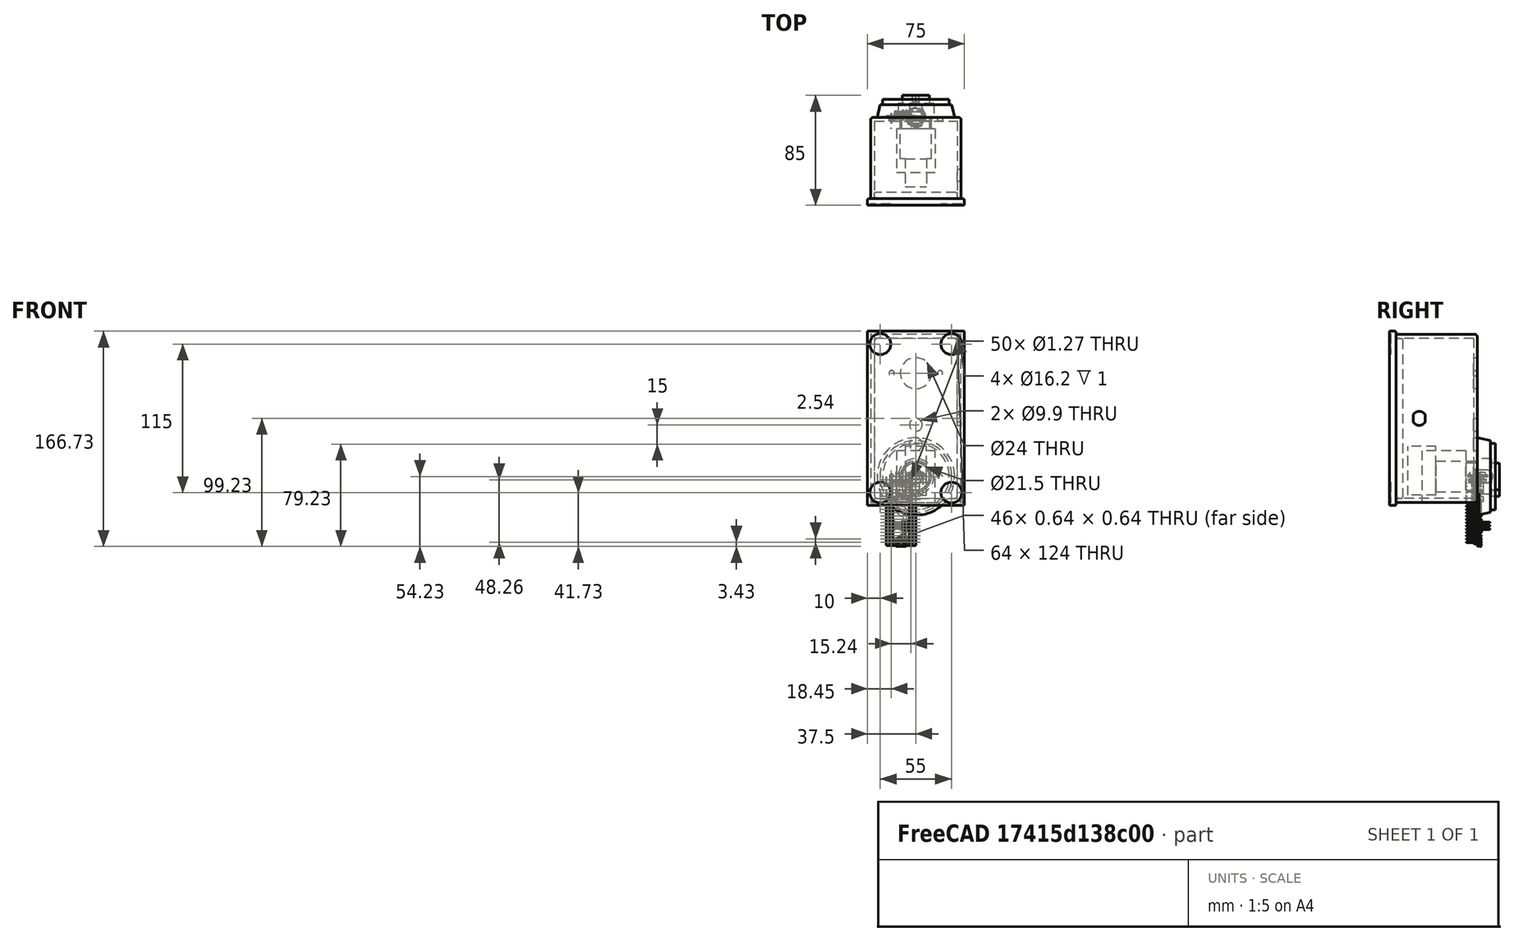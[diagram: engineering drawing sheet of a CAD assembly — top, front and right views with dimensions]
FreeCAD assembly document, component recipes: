
FREECAD ASSEMBLY — COMPONENT RECIPES ("PDU")

This assembly document has 3 components, labeled P0..P2 below (a component is one placed body or linked part). 3 of them carry a construction recipe — the FreeCAD feature program that regenerates the part from scratch, quoted from this document or its linked companion documents; the rest are supplied as boundary geometry only. No exploded tour is included for this assembly.
COMPONENT P0 — recipe-attached ("Rubber", modeled in this document).
Construction recipe (the document's own serialized feature program — sketch geometry with constraints, then the solid features built on it; lengths are millimeters unless a unit is written):

FEATURE [Sketcher::SketchObject] Sketch011
  ArcFitTolerance = 1e-06
  AttachmentSupport = -> [XY_Plane010]
  FullyConstrained = true
  MakeInternals = false
  MapMode = 5
  sketch-geometry (2):
    g0: Circle CenterX=0 CenterY=0 CenterZ=0 NormalX=0 NormalY=0 NormalZ=1 AngleXU=0 Radius=7.75
    g1: Circle CenterX=0 CenterY=0 CenterZ=0 NormalX=0 NormalY=0 NormalZ=1 AngleXU=0 Radius=5.4
  constraints (4):
    c: Diameter(g0) = 15.5
    c: Coincident(g0,g-1)
    c: Diameter(g1) = 10.8
    c: Coincident(g1,g0)
FEATURE [PartDesign::Pad] Pad007
  Direction = (0,0,1)
  Length = 1
  Length2 = 10
  Profile = -> Sketch011
  ReferenceAxis = -> Sketch011 [N_Axis]
  Refine = true
  Suppressed = false
  Type = 0
FEATURE [PartDesign::Body] Body004  label="Rubber"
  AllowCompound = false
  Group = -> [Sketch011,Pad007]
  Origin = -> Origin010
  Tip = -> Pad007
COMPONENT P1 — recipe-attached ("House", modeled in this document).
Construction recipe (the document's own serialized feature program — sketch geometry with constraints, then the solid features built on it; lengths are millimeters unless a unit is written):

FEATURE [Sketcher::SketchObject] Sketch012
  ArcFitTolerance = 1e-06
  FullyConstrained = false
  MakeInternals = false
  sketch-geometry (8):
    g0: ArcOfCircle CenterX=0 CenterY=0 CenterZ=0 NormalX=0 NormalY=0 NormalZ=1 AngleXU=0 Radius=5.4 StartAngle=2.12208 EndAngle=3.14159
    g1: LineSegment StartX=0 StartY=4.6 StartZ=0 EndX=2.82843 EndY=4.6 EndZ=0
    g2: LineSegment StartX=0 StartY=4.6 StartZ=0 EndX=-2.82843 EndY=4.6 EndZ=0
    g3: ArcOfCircle CenterX=0 CenterY=0 CenterZ=0 NormalX=0 NormalY=0 NormalZ=1 AngleXU=0 Radius=5.4 StartAngle=-9e-16 EndAngle=1.01951
    g4: ArcOfCircle CenterX=0 CenterY=0 CenterZ=0 NormalX=0 NormalY=0 NormalZ=1 AngleXU=0 Radius=5.4 StartAngle=3.14159 EndAngle=4.1611
    g5: LineSegment StartX=0 StartY=-4.6 StartZ=0 EndX=-2.82843 EndY=-4.6 EndZ=0
    g6: LineSegment StartX=0 StartY=-4.6 StartZ=0 EndX=2.82843 EndY=-4.6 EndZ=0
    g7: ArcOfCircle CenterX=0 CenterY=0 CenterZ=0 NormalX=0 NormalY=0 NormalZ=1 AngleXU=0 Radius=5.4 StartAngle=5.26367 EndAngle=6.28319
  constraints (14):
    c: Diameter(g0) = 10.8
    c: Coincident(g0,g-1)
    c: PointOnObject(g1,g-2)
    c: Horizontal(g1)
    c: Coincident(g1,g3)
    c: Coincident(g2,g0)
    c: Equal(g0,g3)
    c: Coincident(g0,g3)
    c: Diameter(g4) = 10.8
    c: Horizontal(g6)
    c: Coincident(g6,g7)
    c: Coincident(g5,g4)
    c: Equal(g4,g7)
    c: Coincident(g4,g7)
FEATURE [PartDesign::Pad] Pad008
  Direction = (0,0,1)
  Length = 1
  Length2 = 10
  Profile = -> Sketch012
  ReferenceAxis = -> Sketch012 [N_Axis]
  Refine = true
  Suppressed = false
  Type = 0
FEATURE [Sketcher::SketchObject] Sketch013
  ArcFitTolerance = 1e-06
  FullyConstrained = false
  MakeInternals = false
  sketch-geometry (8):
    g0: ArcOfCircle CenterX=0 CenterY=0 CenterZ=0 NormalX=0 NormalY=0 NormalZ=1 AngleXU=0 Radius=5.4 StartAngle=2.12208 EndAngle=3.14159
    g1: LineSegment StartX=0 StartY=4.6 StartZ=0 EndX=2.82843 EndY=4.6 EndZ=0
    g2: LineSegment StartX=0 StartY=4.6 StartZ=0 EndX=-2.82843 EndY=4.6 EndZ=0
    g3: ArcOfCircle CenterX=0 CenterY=0 CenterZ=0 NormalX=0 NormalY=0 NormalZ=1 AngleXU=0 Radius=5.4 StartAngle=-9e-16 EndAngle=1.01951
    g4: ArcOfCircle CenterX=0 CenterY=0 CenterZ=0 NormalX=0 NormalY=0 NormalZ=1 AngleXU=0 Radius=5.4 StartAngle=3.14159 EndAngle=4.1611
    g5: LineSegment StartX=0 StartY=-4.6 StartZ=0 EndX=-2.82843 EndY=-4.6 EndZ=0
    g6: LineSegment StartX=0 StartY=-4.6 StartZ=0 EndX=2.82843 EndY=-4.6 EndZ=0
    g7: ArcOfCircle CenterX=0 CenterY=0 CenterZ=0 NormalX=0 NormalY=0 NormalZ=1 AngleXU=0 Radius=5.4 StartAngle=5.26367 EndAngle=6.28319
  constraints (14):
    c: Diameter(g0) = 10.8
    c: Coincident(g0,g-1)
    c: PointOnObject(g1,g-2)
    c: Horizontal(g1)
    c: Coincident(g1,g3)
    c: Coincident(g2,g0)
    c: Equal(g0,g3)
    c: Coincident(g0,g3)
    c: Diameter(g4) = 10.8
    c: Horizontal(g6)
    c: Coincident(g6,g7)
    c: Coincident(g5,g4)
    c: Equal(g4,g7)
    c: Coincident(g4,g7)
FEATURE [PartDesign::Pad] Pad009
  BaseFeature = -> Pad008
  Direction = (0,0,1)
  Length = 13.1
  Length2 = 10
  Profile = -> Sketch013
  ReferenceAxis = -> Sketch013 [N_Axis]
  Refine = true
  Reversed = true
  Suppressed = false
  Type = 0
FEATURE [Sketcher::SketchObject] Sketch014
  ArcFitTolerance = 1e-06
  AttachmentSupport = -> [YZ_Plane012]
  FullyConstrained = true
  MakeInternals = false
  MapMode = 5
  Placement = pos=(0,0,0) rot=(0.57735,0.57735,0.57735;2.0944rad)
  sketch-geometry (5):
    g0: LineSegment [constr] StartX=0 StartY=0 StartZ=0 EndX=0 EndY=1 EndZ=0
    g1: LineSegment StartX=0 StartY=1 StartZ=0 EndX=0 EndY=3 EndZ=0
    g2: LineSegment StartX=0 StartY=3 StartZ=0 EndX=5.9 EndY=3 EndZ=0
    g3: LineSegment StartX=0 StartY=1 StartZ=0 EndX=6.9 EndY=1 EndZ=0
    g4: LineSegment StartX=6.9 StartY=1 StartZ=0 EndX=5.9 EndY=3 EndZ=0
  constraints (14):
    c: Distance(g0) = 1
    c: Coincident(g0,g-1)
    c: PointOnObject(g0,g-2)
    c: Distance(g1) = 2
    c: Coincident(g1,g0)
    c: PointOnObject(g1,g-2)
    c: Distance(g2) = 5.9
    c: Coincident(g2,g1)
    c: Horizontal(g2)
    c: Distance(g3) = 6.9
    c: Coincident(g3,g0)
    c: Horizontal(g3)
    c: Coincident(g4,g3)
    c: Coincident(g4,g2)
FEATURE [PartDesign::Revolution] Revolution002
  Angle = 360
  Angle2 = 60
  Axis = (0,0,1)
  Base = (0,0,0)
  BaseFeature = -> Pad009
  Profile = -> Sketch014
  ReferenceAxis = -> Sketch014 [V_Axis]
  Refine = true
  Reversed = true
  Suppressed = false
  Type = 0
FEATURE [Sketcher::SketchObject] Sketch015
  ArcFitTolerance = 1e-06
  AttachmentSupport = -> [Revolution002]
  FullyConstrained = false
  MakeInternals = false
  MapMode = 5
  Placement = pos=(0,0,3) rot=(0,0,1;0rad)
  sketch-geometry (4):
    g0: ArcOfCircle CenterX=-3.315 CenterY=-8.55e-14 CenterZ=0 NormalX=0 NormalY=0 NormalZ=1 AngleXU=0 Radius=1.28 StartAngle=1.5708 EndAngle=4.71239
    g1: ArcOfCircle CenterX=3.315 CenterY=-8.55e-14 CenterZ=0 NormalX=0 NormalY=0 NormalZ=1 AngleXU=0 Radius=1.28 StartAngle=4.71239 EndAngle=7.85398
    g2: LineSegment StartX=-3.315 StartY=1.28 StartZ=0 EndX=3.315 EndY=1.28 EndZ=0
    g3: LineSegment StartX=-3.315 StartY=-1.28 StartZ=0 EndX=3.315 EndY=-1.28 EndZ=0
  constraints (9):
    c: PointOnObject(g0,g-1)
    c: Tangent(g0,g2) = 1.5708
    c: Tangent(g0,g3) = -1.5708
    c: Tangent(g1,g2) = 1.5708
    c: Tangent(g1,g3) = -1.5708
    c: Equal(g0,g1)
    c: Horizontal(g3)
    c: Distance(g0,g1) = 6.63
    c: Radius(g0) = 1.28
FEATURE [PartDesign::Pocket] Pocket001
  BaseFeature = -> Revolution002
  Direction = (0,0,-1)
  Length = 1
  Length2 = 5
  Profile = -> Sketch015
  ReferenceAxis = -> Sketch015 [N_Axis]
  Refine = true
  Suppressed = false
  Type = 0
FEATURE [PartDesign::Body] Body005  label="House"
  AllowCompound = false
  Group = -> [Sketch012,Sketch013,Pad008,Pad009,Sketch014,Revolution002,Sketch015,Pocket001]
  Origin = -> Origin012
  Tip = -> Pocket001
COMPONENT P2 — recipe-attached ("Skrew", modeled in this document).
Construction recipe (the document's own serialized feature program — sketch geometry with constraints, then the solid features built on it; lengths are millimeters unless a unit is written):

FEATURE [Sketcher::SketchObject] Sketch016
  ArcFitTolerance = 1e-06
  AttachmentSupport = -> [XY_Plane013]
  FullyConstrained = true
  MakeInternals = false
  MapMode = 5
  sketch-geometry (8):
    g0: LineSegment StartX=7.75 StartY=0 StartZ=0 EndX=3.875 EndY=6.7117 EndZ=0
    g1: LineSegment StartX=3.875 StartY=6.7117 StartZ=0 EndX=-3.875 EndY=6.7117 EndZ=0
    g2: LineSegment StartX=-3.875 StartY=6.7117 StartZ=0 EndX=-7.75 EndY=9e-16 EndZ=0
    g3: LineSegment StartX=-7.75 StartY=9e-16 StartZ=0 EndX=-3.875 EndY=-6.7117 EndZ=0
    g4: LineSegment StartX=-3.875 StartY=-6.7117 StartZ=0 EndX=3.875 EndY=-6.7117 EndZ=0
    g5: LineSegment StartX=3.875 StartY=-6.7117 StartZ=0 EndX=7.75 EndY=0 EndZ=0
    g6: Circle [constr] CenterX=0 CenterY=0 CenterZ=0 NormalX=0 NormalY=0 NormalZ=1 AngleXU=0 Radius=7.75
    g7: Circle CenterX=0 CenterY=0 CenterZ=0 NormalX=0 NormalY=0 NormalZ=1 AngleXU=0 Radius=5.4
  constraints (18):
    c: Coincident(g0,g1)
    c: Coincident(g1,g2)
    c: Coincident(g2,g3)
    c: Coincident(g3,g4)
    c: Coincident(g4,g5)
    c: Coincident(g5,g0)
    c: Equal(g0, g1-g5) x5
    c: PointOnObject(g0,g6)
    c: PointOnObject(g1,g6)
    c: PointOnObject(g2,g6)
    c: PointOnObject(g3,g6)
    c: PointOnObject(g4,g6)
    c: PointOnObject(g5,g6)
    c: Radius(g6) = 7.75
    c: Coincident(g6,g-1)
    c: PointOnObject(g5,g-1)
    c: Diameter(g7) = 10.8
    c: Coincident(g7,g6)
FEATURE [PartDesign::Pad] Pad010
  Direction = (0,0,1)
  Length = 3
  Length2 = 10
  Profile = -> Sketch016
  ReferenceAxis = -> Sketch016 [N_Axis]
  Refine = true
  Reversed = true
  Suppressed = false
  Type = 0
FEATURE [PartDesign::Body] Body006  label="Skrew"
  AllowCompound = false
  Group = -> [Sketch016,Pad010]
  Origin = -> Origin013
  Placement = pos=(0,0,-2) rot=(0,0,1;0rad)
  Tip = -> Pad010
PROVENANCE & LICENSES
A FreeCAD (.FCStd) document from a public repository crawl; recipes are the document's own serialized feature recipes (and, for linked parts, companion documents' recipes).
License: as declared in the source repository (recorded in the dataset sidecar).
